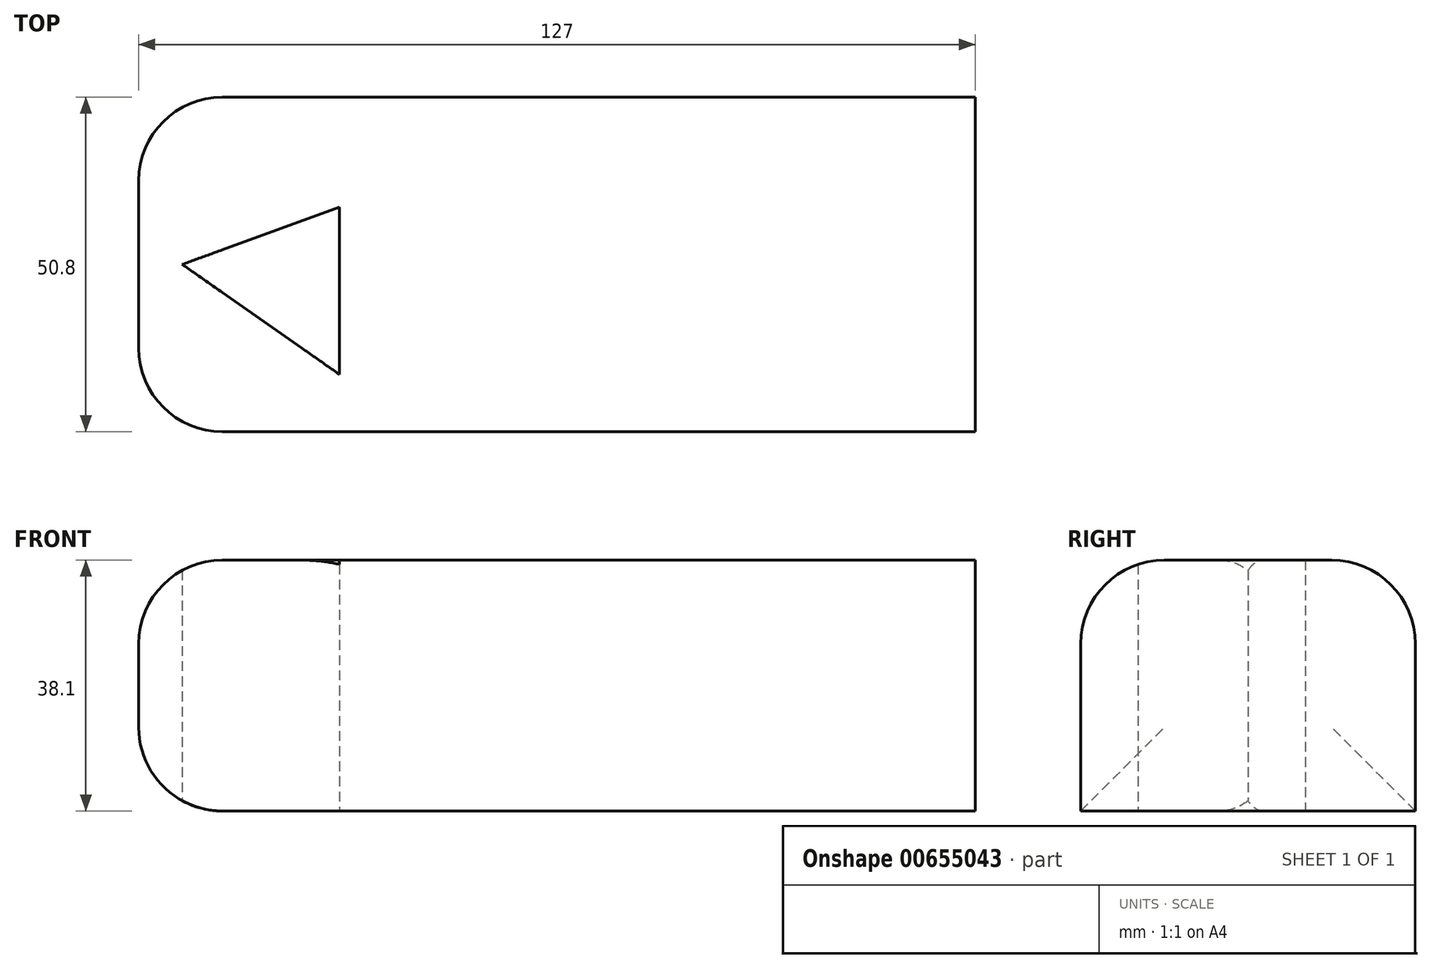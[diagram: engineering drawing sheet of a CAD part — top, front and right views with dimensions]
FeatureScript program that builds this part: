
annotation { "Feature Type Name" : "Feature", "Feature Type Description" : "" }
export const myFeature = defineFeature(function(context is Context, id is Id, definition is map)
    precondition{}
    {
        {
            var Q0;
            Q0=qCreatedBy(makeId("Top.planeOp"),FACE);
            var sketch = newSketch(context, id + "F0", { "sketchPlane" : qUnion([Q0])});
            skLineSegment(sketch, "E0.bottom", {"start": v(-59.1, 25.4) * mm, "end": v(67.9, 25.4) * mm});
            skLineSegment(sketch, "E0.top", {"start": v(-59.1, -25.4) * mm, "end": v(67.9, -25.4) * mm});
            skLineSegment(sketch, "E0.left", {"start": v(-59.1, 25.4) * mm, "end": v(-59.1, -25.4) * mm});
            skLineSegment(sketch, "E0.right", {"start": v(67.9, 25.4) * mm, "end": v(67.9, -25.4) * mm});
            skLineSegment(sketch, "E1", {"start": v(-52.5, 0) * mm, "end": v(-28.62, 8.69) * mm});
            skLineSegment(sketch, "E2", {"start": v(-28.62, 8.69) * mm, "end": v(-28.62, -16.71) * mm});
            skLineSegment(sketch, "E3", {"start": v(-28.62, -16.71) * mm, "end": v(-52.5, 0) * mm});
            skSolve(sketch);
        }
        {
            var Q0;
            Q0=makeQuery(id+"F0.imprint","IMPRINT",FACE,{"disambiguationData":[TD([[makeQuery(id+"F0.imprint","IMPRINT",EDGE,{"derivedFrom":sQuery(id+"F0.wireOp",EDGE,"E0.bottom")}),-1.0]])]});
            extrude(context, id + "F1", {"entities" : qUnion([Q0]), "depth" : 38.1 * mm, "offsetDistance" : 25.4 * mm});
        }
        {
            var Q0;
            Q0=makeQuery(id+"F1.opExtrude","SWEPT_FACE",FACE,{"disambiguationData":[OSD([sQuery(id+"F0.wireOp",EDGE,"E0.left")])]});
            var Q1;
            Q1=makeQuery(id+"F1.opExtrude","CAP_EDGE",EDGE,{"disambiguationData":[OSD([sQuery(id+"F0.wireOp",EDGE,"E0.top")])],"isStart":false});
            var Q2;
            Q2=makeQuery(id+"F1.opExtrude","CAP_EDGE",EDGE,{"disambiguationData":[OSD([sQuery(id+"F0.wireOp",EDGE,"E0.bottom")])],"isStart":false});
            fillet(context, id + "F2", {"entities" : qUnion([Q0, Q1, Q2]), "radius" : 12.7 * mm, "tangentPropagation" : true, "allowEdgeOverflow" : false});
        }
    });
